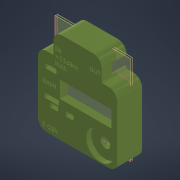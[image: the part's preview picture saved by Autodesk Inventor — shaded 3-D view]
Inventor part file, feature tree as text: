
AUTODESK INVENTOR PART (.ipt)
format: ipt  version: 2022 (Build 260153000, 153)  size: 1,149,440 bytes
history: native  units: in
note: dims shown in document units (in); Inventor stores cm internally (conversion verified against a paired STEP export)
features: reference x22, extrude x13, sketch x13, projected_geometry x11, other x6, chamfer x1
ambient origin geometry x8: Origin, YZ Plane, XZ Plane, XY Plane, X Axis, Y Axis, Z Axis, Center Point
bodies: Solid1 (feature_tree)
feature tree (66):
  other  "board backside"
  extrude  "side walls"  Depth=0.2673in
  extrude  "front cutouts"  Depth=0.1575in
  extrude  "power jack cutout"  Depth=0.0591in
  extrude  "rf connector cutouts"  Depth=0.0591in
  extrude  "Extrusion8"  Depth=0.2673in
  other  "board frontside"
  extrude  "board support standoffs"  Depth=0.0197in
  sketch  "Sketch14"  dims[d22=0.0669in d23=0.0945in]
  extrude  "Extrusion14"  Depth=0.0197in
  extrude  "encoder knob hole"  Depth=0.0197in
  other  "Work Point1"
  extrude  "Extrusion11"  Depth=0.2362in TaperAngle=0.0deg
  extrude  "Extrusion12"  Depth=0.0945in
  chamfer  "Chamfer2"  Distance=0.0394in
  extrude  "Extrusion15"  TaperAngle=0.0deg  [1 undecoded]
  extrude  "Extrusion16"  TaperAngle=0.0deg  [1 undecoded]
  extrude  "Extrusion17"  Depth=0.4921in TaperAngle=0.0deg
  sketch  "Sketch1"  dims[d0=0.0059in d3=0.2673in]
  reference  "Reference1"
  sketch  "Sketch2"  dims[d4=0.1575in d5=0.1575in]
  projected_geometry  "Projected Loop1"
  reference  "Reference2"
  reference  "Reference3"
  reference  "Reference4"
  reference  "Reference5"
  reference  "Reference6"
  reference  "Reference7"
  sketch  "Sketch3"  dims[d6=0.0394in d7=0.0591in]
  reference  "Reference8"
  reference  "Reference9"
  reference  "Reference10"
  reference  "Reference11"
  reference  "Reference12"
  reference  "Reference13"
  reference  "Reference14"
  reference  "Reference15"
  reference  "Reference16"
  reference  "Reference17"
  sketch  "Sketch6"  dims[d8=0.0591in d9=0.0591in]
  projected_geometry  "Projected Loop4"
  reference  "Reference27"
  sketch  "Sketch7"  dims[d10=0.0591in d11=0.2673in]
  projected_geometry  "Projected Loop5"
  projected_geometry  "Projected Loop6"
  sketch  "Sketch8"  dims[d12=0.5315in d13=0.0in d14=0.0197in]
  projected_geometry  "Projected Loop7"
  projected_geometry  "Projected Loop8"
  projected_geometry  "Projected Loop9"
  projected_geometry  "Projected Loop10"
  reference  "Reference28"
  reference  "Reference29"
  reference  "Reference30"
  sketch  "Sketch9"  dims[d15=0.0079in d16=0.0197in]
  sketch  "Sketch10"  dims[d17=0.0197in d18=0.0197in]
  sketch  "Sketch11"  dims[d19=0.2953in d20=0.2362in d21=0.0in]
  projected_geometry  "Projected Loop13"
  projected_geometry  "Projected Loop14"
  projected_geometry  "Projected Loop15"
  reference  "Reference32"
  sketch  "Sketch15"  dims[d24=0.0472in]
  sketch  "Sketch16"  dims[d25=0.0492in]
  sketch  "Sketch17"  dims[d26=0.1181in d27=0.0394in d28=0.0in d29=0.0in d33=0.4921in d34=0.0in d43=0.1575in d44=0.1575in d45=0.2165in d46=0.0in d50=0.2362in d51=0.0in d52=0.0591in d53=0.5906in d54=0.0591in d55=0.1969in d56=0.1969in d57=0.0591in d58=0.0591in d59=0.0591in d60=0.0591in d61=0.3937in d62=0.0591in d63=0.7874in d64=0.0591in d65=0.6299in d66=0.3543in d67=0.0591in d68=0.3937in d69=0.0591in d70=0.0591in d71=0.5079in d72=0.0in d73=0.3543in d74=0.0787in d75=0.0787in d76=0.8701in d77=0.1575in d78=0.0in d83=0.0591in d84=0.1575in d85=0.0in d93=0.2611in d94=0.2611in d96=0.0591in d97=0.3937in d99=0.0512in d100=0.0512in d101=0.0787in d102=0.0in d106=0.3937in d107=0.0in d108=0.0394in d109=0.2611in d110=0.2611in d111=0.0591in d112=0.0591in d113=0.0197in d114=0.0787in d115=45.0deg d117=0.1181in d118=0.1181in d121=0.0787in d122=0.0in d124=0.3937in d125=0.0551in d126=0.0472in d127=0.2756in d128=0.315in d129=0.0787in d130=0.7087in d131=0.315in d132=0.0in d133=0.0in d134=0.0394in d135=0.0in]
  parser-record x1  (decoder bookkeeping rows leaked as tree rows — omitted from the tree; the rows remain in map.json)
  other  "case_assembly.iam"
  other  "rf-vga:1"
note: 2 required parameter values undecoded (feature->parameter linkage not recoverable at this tier; creation-order binding heuristic only, values carry confidence <= 0.55)
note: 1 file-system path scrubbed to <path> (originals preserved in map.json)
